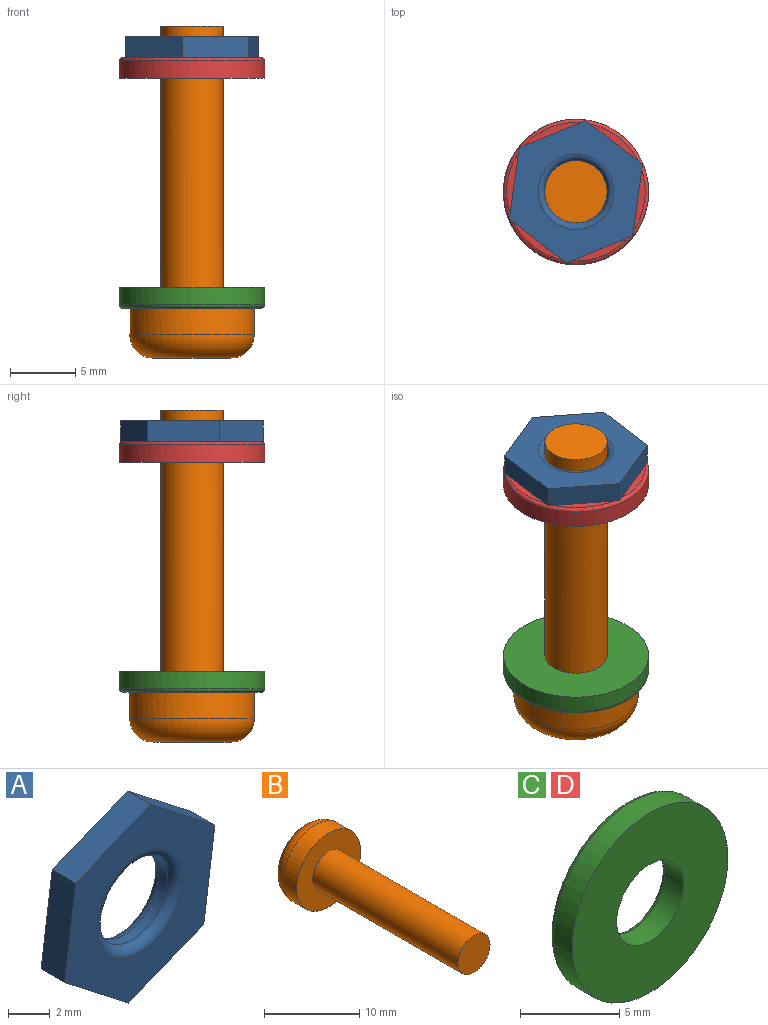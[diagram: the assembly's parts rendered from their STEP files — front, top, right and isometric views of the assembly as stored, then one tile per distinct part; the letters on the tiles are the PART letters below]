
ASSEMBLY  parts=4 mates=3
PART A: 11 faces, bbox 10.2x1.6x10.9 mm
  f0: plane 5.45x1.59mm, normal (-0.99,0,0.14), area 8.7mm2, adj f1,f6,f7,f8
  f1: plane 4.34x3.38mm, normal (-0.61,0,-0.79), area 8.7mm2, adj f0,f2,f7,f8
  f2: plane 5.09x2.07mm, normal (0.38,0,-0.93), area 8.7mm2, adj f1,f3,f7,f8
  f3: plane 5.45x1.59mm, normal (0.99,0,-0.14), area 8.7mm2, adj f2,f4,f7,f8
  f4: plane 4.34x3.38mm, normal (0.61,0,0.79), area 8.7mm2, adj f3,f6,f7,f8
  f5: cylinder r=2.38mm len=4.76mm, axis (0,1,0), area 8.6mm2, adj f9,f10
  f6: plane 5.09x2.07mm, normal (-0.38,0,0.93), area 8.7mm2, adj f0,f4,f7,f8
  f7: plane 10.9x10.19mm, normal (0,-1,0), area 52.3mm2, adj f0,f1,f2,f3,f4,f6,f9
  f8: plane 10.9x10.19mm, normal (0,1,0), area 52.3mm2, adj f0,f1,f2,f3,f4,f6,f10
  f9: torus R=2.89mm, axis (0,-1,0), area 12.9mm2, adj f5,f7
  f10: torus R=2.89mm, axis (0,-1,0), area 12.9mm2, adj f5,f8
PART B: 19 faces, bbox 10.3x25.4x10.3 mm
  f0: plane 5.97x5.97mm, normal (0,1,0), area 15.4mm2, adj f1,f2,f7,f8,f9,f10,f12,f13
  f1: plane 1.59x0.76mm, normal (0,0,-1), area 1.2mm2, adj f0,f8,f11,f17
  f2: plane 1.59x0.76mm, normal (0,0,1), area 1.2mm2, adj f0,f8,f11,f13
  f3: cylinder r=4.76mm len=9.53mm, axis (0,1,0), area 60.8mm2, adj f4,f18
  f4: plane 9.53x9.53mm, normal (0,-1,0), area 53.4mm2, adj f3,f5
  f5: cylinder r=2.38mm len=21.59mm, axis (0,1,0), area 323mm2, adj f4,f6
  f6: plane 4.76x4.76mm, normal (0,-1,0), area 17.8mm2, adj f5
  f7: plane 1.59x0.76mm, normal (0,0,-1), area 1.2mm2, adj f0,f10,f11,f15
  f8: plane 1.59x0.76mm, normal (-1,0,0), area 1.2mm2, adj f0,f1,f2,f11
  f9: plane 1.59x0.76mm, normal (0,0,1), area 1.2mm2, adj f0,f10,f11,f12
  f10: plane 1.59x0.76mm, normal (1,0,0), area 1.2mm2, adj f0,f7,f9,f11
  f11: plane 4.76x4.76mm, normal (0,1,0), area 12.6mm2, adj f1,f2,f7,f8,f9,f10,f12,f13
  f12: plane 1.59x0.76mm, normal (1,0,0), area 1.2mm2, adj f0,f9,f11,f14
  f13: plane 1.59x0.76mm, normal (-1,0,0), area 1.2mm2, adj f0,f2,f11,f14
  f14: plane 1.59x0.76mm, normal (0,0,1), area 1.2mm2, adj f0,f11,f12,f13
  f15: plane 1.59x0.76mm, normal (1,0,0), area 1.2mm2, adj f0,f7,f11,f16
  f16: plane 1.59x0.76mm, normal (0,0,-1), area 1.2mm2, adj f0,f11,f15,f17
  f17: plane 1.59x0.76mm, normal (-1,0,0), area 1.2mm2, adj f0,f1,f11,f16
  f18: torus R=2.98mm, axis (0,-1,0), area 72.2mm2, adj f0,f3
PART C: 6 faces, bbox 12x1.6x12 mm
  f0: cylinder r=5.56mm len=11.11mm, axis (0,1,0), area 46.6mm2, adj f1,f5
  f1: plane 11.11x11.11mm, normal (0,-1,0), area 79.2mm2, adj f0,f3
  f2: plane 10.6x10.6mm, normal (0,1,0), area 66.5mm2, adj f4,f5
  f3: cylinder r=2.38mm len=4.76mm, axis (0,-1,0), area 20mm2, adj f1,f4
  f4: torus R=2.64mm, axis (0,-1,0), area 6.2mm2, adj f2,f3
  f5: torus R=5.3mm, axis (0,-1,0), area 13.7mm2, adj f0,f2
PART D: same geometry as C
PLACE A rot(axis=(-1,0,0),90deg) t=(0,0,-1.62)mm
PLACE B rot(axis=(-1,0,0),90deg) t=(0,0,-25.4)mm
PLACE C rot(axis=(-1,0,0),90deg) t=(0,0,-20.8)mm
PLACE D rot(axis=(1,0,0),90deg) t=(0,0,-3.21)mm
MATE fastened A.f5 <-> D.f0  axis (0,0,-1) through (0,0,-2.41)mm
MATE fastened D.f0 <-> C.f0  axis (0,0,-1) through (0,0,-4)mm
MATE fastened C.f0 <-> B.f3  axis (0,0,-1) through (0,0,-21.59)mm
